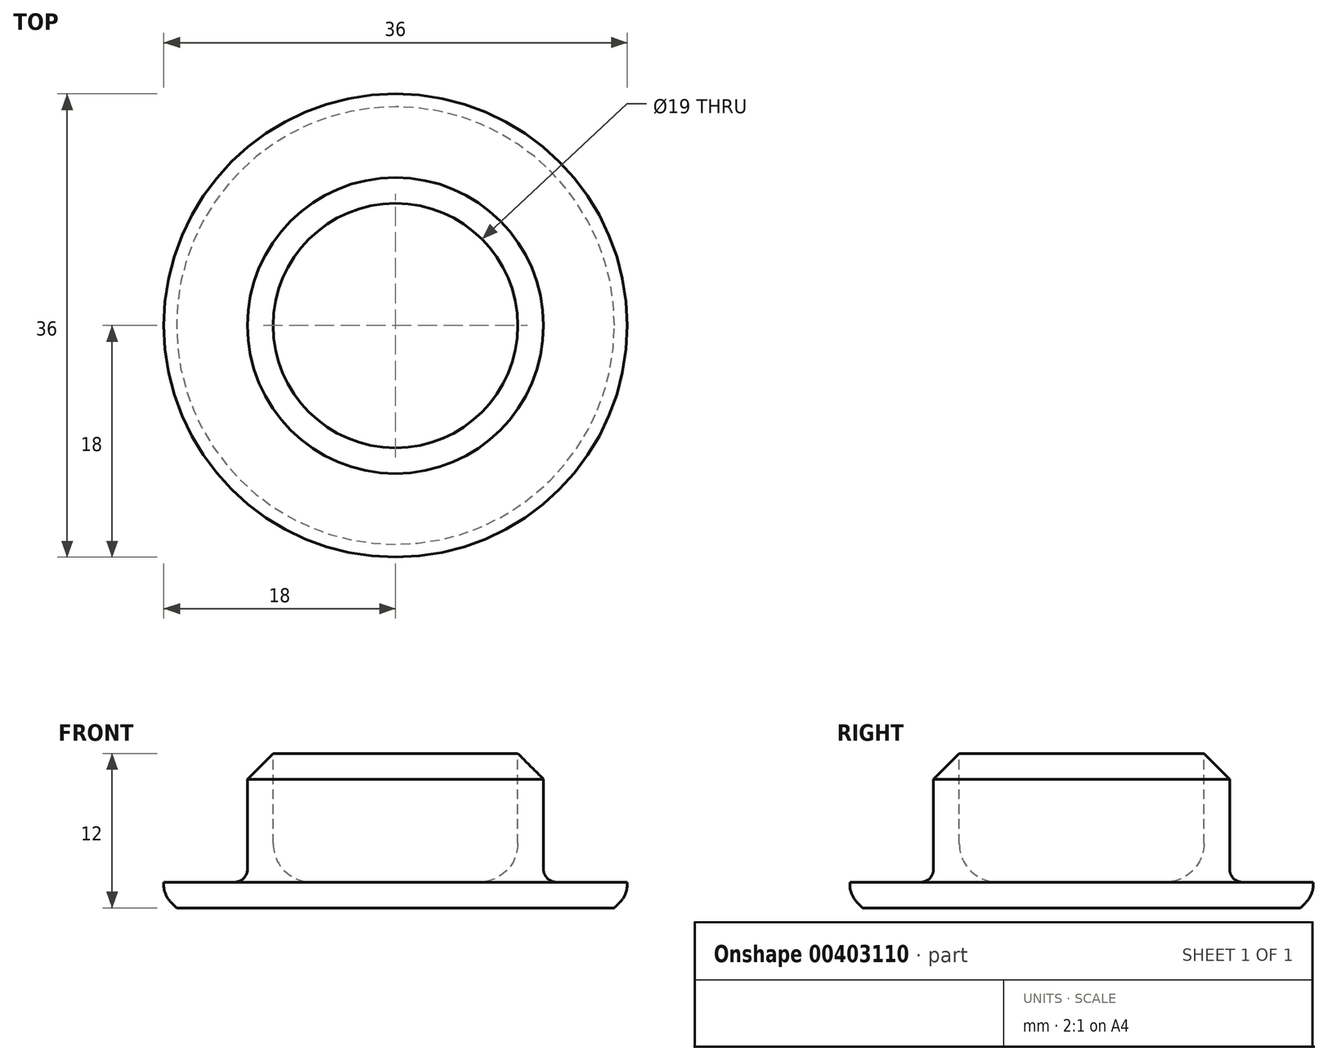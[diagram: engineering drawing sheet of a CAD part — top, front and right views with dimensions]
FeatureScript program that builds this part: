
annotation { "Feature Type Name" : "Feature", "Feature Type Description" : "" }
export const myFeature = defineFeature(function(context is Context, id is Id, definition is map)
    precondition{}
    {
        {
            var Q0;
            Q0=qCreatedBy(makeId("Front.planeOp"),FACE);
            var sketch = newSketch(context, id + "F0", { "sketchPlane" : qUnion([Q0])});
            skLineSegment(sketch, "E0", {"start": v(0, 0) * mm, "end": v(17, 0) * mm});
            skLineSegment(sketch, "E1", {"start": v(17, 0) * mm, "end": v(18, 1) * mm});
            skLineSegment(sketch, "E2", {"start": v(18, 1) * mm, "end": v(18, 2) * mm});
            skLineSegment(sketch, "E3", {"start": v(18, 2) * mm, "end": v(11.5, 2) * mm});
            skLineSegment(sketch, "E4", {"start": v(11.5, 2) * mm, "end": v(11.5, 10) * mm});
            skLineSegment(sketch, "E5", {"start": v(11.5, 10) * mm, "end": v(9.5, 12) * mm});
            skLineSegment(sketch, "E6", {"start": v(9.5, 12) * mm, "end": v(9.5, 2) * mm});
            skLineSegment(sketch, "E7", {"start": v(9.5, 2) * mm, "end": v(0, 2) * mm});
            skLineSegment(sketch, "E8", {"start": v(0, 2) * mm, "end": v(0, 0) * mm});
            skSolve(sketch);
        }
        {
            var Q0;
            Q0=makeQuery(id+"F0.imprint","IMPRINT",FACE,{"disambiguationData":[TD([[makeQuery(id+"F0.imprint","IMPRINT",EDGE,{"derivedFrom":sQuery(id+"F0.wireOp",EDGE,"E0")}),1.0]])]});
            var Q1;
            Q1=sQuery(id+"F0.wireOp",EDGE,"E8");
            revolve(context, id + "F1", {"entities" : qUnion([Q0]), "axis" : qUnion([Q1]), "revolveType" : RevolveType.FULL});
        }
        {
            var Q0;
            Q0=makeQuery(id+"F1.opRevolve","SWEPT_EDGE",EDGE,{"disambiguationData":[OSD([sQuery(id+"F0.wireOp",EDGE,"E6"),sQuery(id+"F0.wireOp",EDGE,"E7")])]});
            fillet(context, id + "F2", {"entities" : qUnion([Q0]), "radius" : 3 * mm, "tangentPropagation" : true, "allowEdgeOverflow" : false});
        }
        {
            var Q0;
            Q0=makeQuery(id+"F1.opRevolve","SWEPT_EDGE",EDGE,{"disambiguationData":[OSD([sQuery(id+"F0.wireOp",EDGE,"E1"),sQuery(id+"F0.wireOp",EDGE,"E2")])]});
            fillet(context, id + "F3", {"entities" : qUnion([Q0]), "radius" : 2 * mm, "tangentPropagation" : true, "allowEdgeOverflow" : false});
        }
        {
            var Q0;
            Q0=makeQuery(id+"F1.opRevolve","SWEPT_EDGE",EDGE,{"disambiguationData":[OSD([sQuery(id+"F0.wireOp",EDGE,"E3"),sQuery(id+"F0.wireOp",EDGE,"E4")])]});
            fillet(context, id + "F4", {"entities" : qUnion([Q0]), "radius" : 1 * mm, "tangentPropagation" : true, "allowEdgeOverflow" : false});
        }
    });
